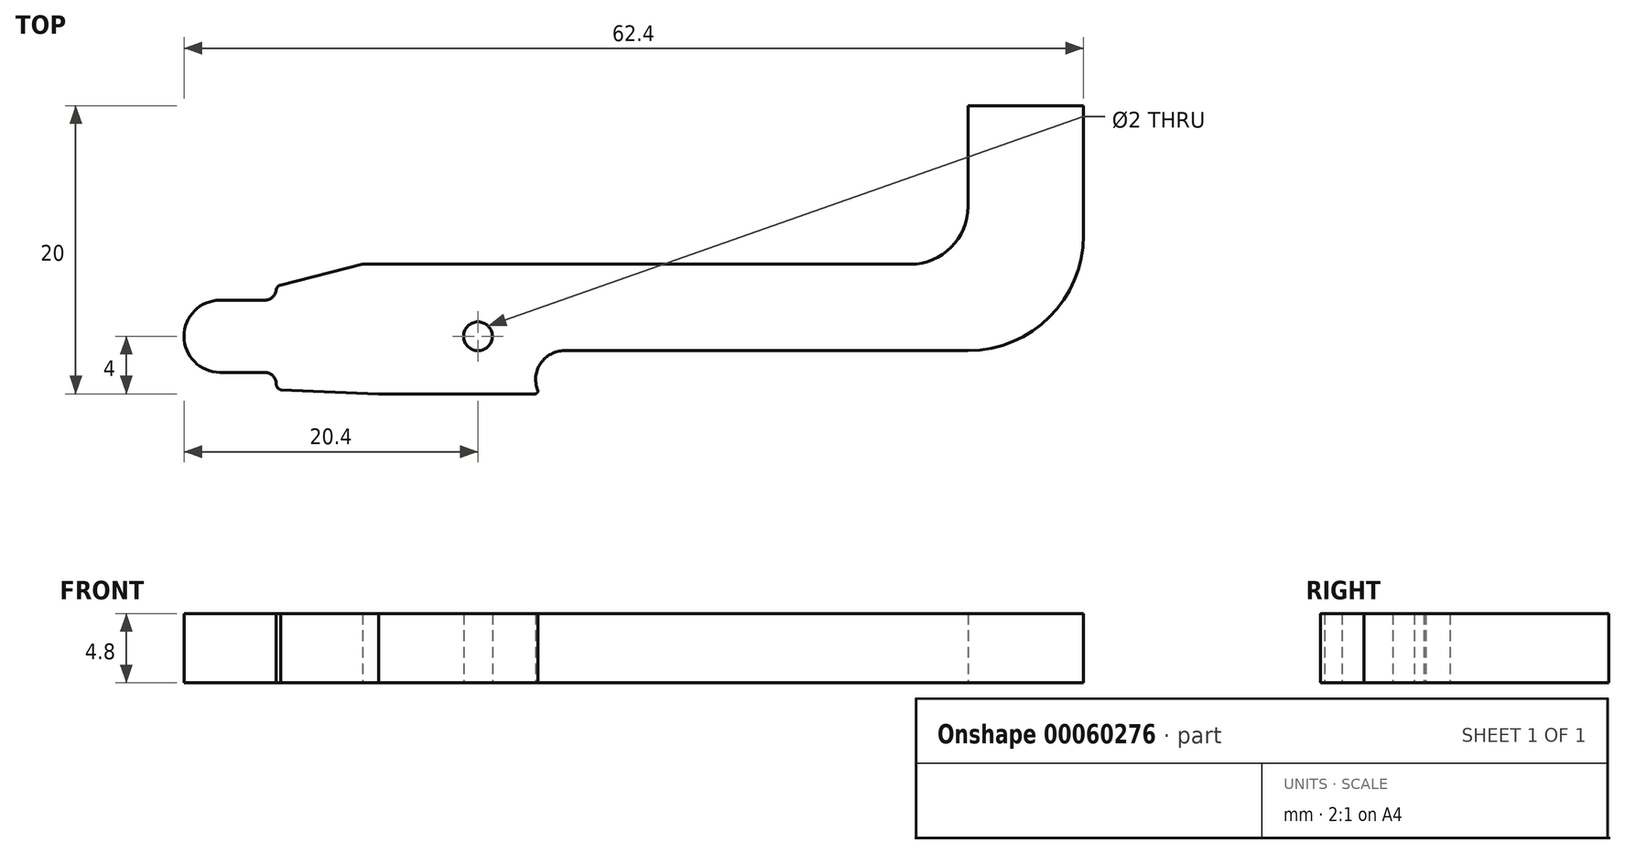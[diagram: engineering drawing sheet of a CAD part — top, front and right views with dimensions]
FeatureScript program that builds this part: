
annotation { "Feature Type Name" : "Feature", "Feature Type Description" : "" }
export const myFeature = defineFeature(function(context is Context, id is Id, definition is map)
    precondition{}
    {
        {
            var Q0;
            Q0=qCreatedBy(makeId("Top.planeOp"),FACE);
            var sketch = newSketch(context, id + "F0", { "sketchPlane" : qUnion([Q0])});
            skLineSegment(sketch, "E0", {"start": v(59.9, 12) * mm, "end": v(59.9, 21) * mm});
            skLineSegment(sketch, "E1", {"start": v(59.9, 21) * mm, "end": v(51.9, 21) * mm});
            skLineSegment(sketch, "E2", {"start": v(51.9, 21) * mm, "end": v(51.9, 14) * mm});
            skLineSegment(sketch, "E3", {"start": v(47.9, 10) * mm, "end": v(9.9, 10) * mm});
            skPoint(sketch, "E4.visualSharp", {"position": v(59.9, 0) * mm});
            skPoint(sketch, "E5.visualSharp", {"position": v(51.9, 10) * mm});
            skArc(sketch, "E5.filletArc", {"start": v(47.9, 10) * mm, "mid": v(50.73, 11.17) * mm, "end": v(51.9, 14) * mm});
            skLineSegment(sketch, "E6", {"start": v(59.9, 15) * mm, "end": v(17.9, 15) * mm, "construction": true});
            skLineSegment(sketch, "E7", {"start": v(17.9, 15) * mm, "end": v(17.9, -7.71) * mm, "construction": true});
            skLineSegment(sketch, "E8", {"start": v(0, 5) * mm, "end": v(54.82, 5) * mm, "construction": true});
            skCircle(sketch, "E9", {"center": v(17.9, 5) * mm, "radius": 1 * mm});
            skArc(sketch, "E10", {"start": v(0, 7.5) * mm, "mid": v(-2.5, 5) * mm, "end": v(0, 2.5) * mm});
            skLineSegment(sketch, "E11", {"start": v(9.9, -2.16) * mm, "end": v(9.9, 16.4) * mm, "construction": true});
            skLineSegment(sketch, "E12", {"start": v(4.2, 8.56) * mm, "end": v(9.9, 10) * mm});
            skPoint(sketch, "E13.orphan", {"position": v(0, 0) * mm});
            skPoint(sketch, "E14.orphan", {"position": v(0, 10) * mm});
            skLineSegment(sketch, "E15", {"start": v(23.9, 15) * mm, "end": v(23.9, -7.92) * mm, "construction": true});
            skLineSegment(sketch, "E16", {"start": v(23.9, 4) * mm, "end": v(51.9, 4) * mm});
            skArc(sketch, "E17", {"start": v(23.9, 4) * mm, "mid": v(22.25, 3.13) * mm, "end": v(22.04, 1.27) * mm});
            skPoint(sketch, "E17.endSnap0", {"position": v(23.9, 3.54) * mm});
            skPoint(sketch, "E18.visualSharp", {"position": v(23.9, 0) * mm});
            skArc(sketch, "E19.filletArc", {"start": v(51.9, 4) * mm, "mid": v(57.56, 6.34) * mm, "end": v(59.9, 12) * mm});
            skLineSegment(sketch, "E20", {"start": v(3.9, 14.19) * mm, "end": v(3.9, -5.44) * mm, "construction": true});
            skLineSegment(sketch, "E21", {"start": v(0, 2.5) * mm, "end": v(3.1, 2.5) * mm});
            skLineSegment(sketch, "E22", {"start": v(0, 7.5) * mm, "end": v(3.1, 7.5) * mm});
            skLineSegment(sketch, "E23", {"start": v(3.9, 8.17) * mm, "end": v(3.9, 8.3) * mm});
            skLineSegment(sketch, "E24", {"start": v(3.9, 1.7) * mm, "end": v(3.9, 1.68) * mm});
            skPoint(sketch, "E25.visualSharp", {"position": v(3.9, 7.5) * mm});
            skArc(sketch, "E25.filletArc", {"start": v(3.1, 7.5) * mm, "mid": v(3.67, 7.73) * mm, "end": v(3.9, 8.3) * mm});
            skPoint(sketch, "E26.visualSharp", {"position": v(3.9, 2.5) * mm});
            skArc(sketch, "E26.filletArc", {"start": v(3.9, 1.7) * mm, "mid": v(3.67, 2.27) * mm, "end": v(3.1, 2.5) * mm});
            skPoint(sketch, "E27.visualSharp", {"position": v(3.9, 1.36) * mm});
            skArc(sketch, "E27.filletArc", {"start": v(3.9, 1.68) * mm, "mid": v(3.99, 1.43) * mm, "end": v(4.21, 1.3) * mm});
            skPoint(sketch, "E28.visualSharp", {"position": v(3.9, 8.48) * mm});
            skArc(sketch, "E28.filletArc", {"start": v(4.2, 8.56) * mm, "mid": v(3.98, 8.42) * mm, "end": v(3.9, 8.17) * mm});
            skLineSegment(sketch, "E29.0", {"start": v(11, 1) * mm, "end": v(21.85, 1) * mm});
            skLineSegment(sketch, "E30", {"start": v(4.21, 1.3) * mm, "end": v(11, 1) * mm});
            skPoint(sketch, "E31.visualSharp", {"position": v(22.17, 1) * mm});
            skArc(sketch, "E31.filletArc", {"start": v(21.85, 1) * mm, "mid": v(22.02, 1.09) * mm, "end": v(22.04, 1.27) * mm});
            skSolve(sketch);
        }
        {
            var Q0;
            Q0=makeQuery(id+"F0.imprint","IMPRINT",FACE,{"disambiguationData":[TD([[makeQuery(id+"F0.imprint","IMPRINT",EDGE,{"derivedFrom":sQuery(id+"F0.wireOp",EDGE,"E0")}),1.0]])]});
            extrude(context, id + "F1", {"entities" : qUnion([Q0]), "depth" : 4.8 * mm});
        }
    });
